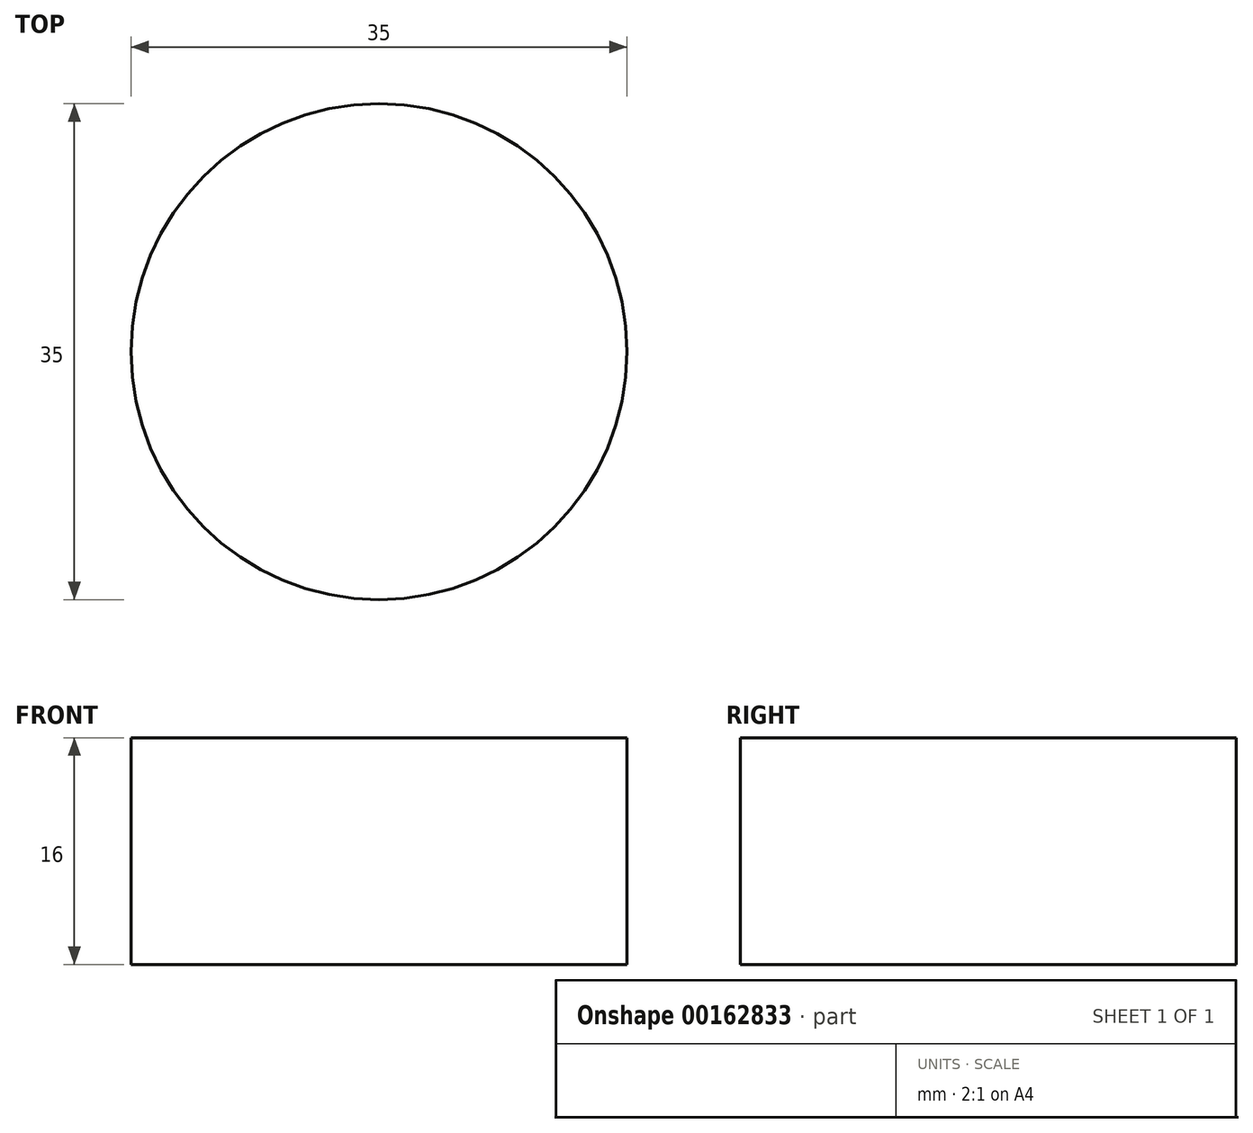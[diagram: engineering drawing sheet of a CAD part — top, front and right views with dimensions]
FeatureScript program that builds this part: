
annotation { "Feature Type Name" : "Feature", "Feature Type Description" : "" }
export const myFeature = defineFeature(function(context is Context, id is Id, definition is map)
    precondition{}
    {
        {
            var Q0;
            Q0=qCreatedBy(makeId("Top.planeOp"),FACE);
            var sketch = newSketch(context, id + "F0", { "sketchPlane" : qUnion([Q0])});
            skCircle(sketch, "E0", {"center": v(0, 0) * mm, "radius": 17.5 * mm});
            skSolve(sketch);
        }
        {
            var Q0;
            Q0=makeQuery(id+"F0.imprint","IMPRINT",FACE,{"disambiguationData":[TD([[makeQuery(id+"F0.imprint","IMPRINT",EDGE,{"derivedFrom":sQuery(id+"F0.wireOp",EDGE,"E0")}),1.0]])]});
            extrude(context, id + "F1", {"entities" : qUnion([Q0]), "depth" : 16 * mm});
        }
    });
